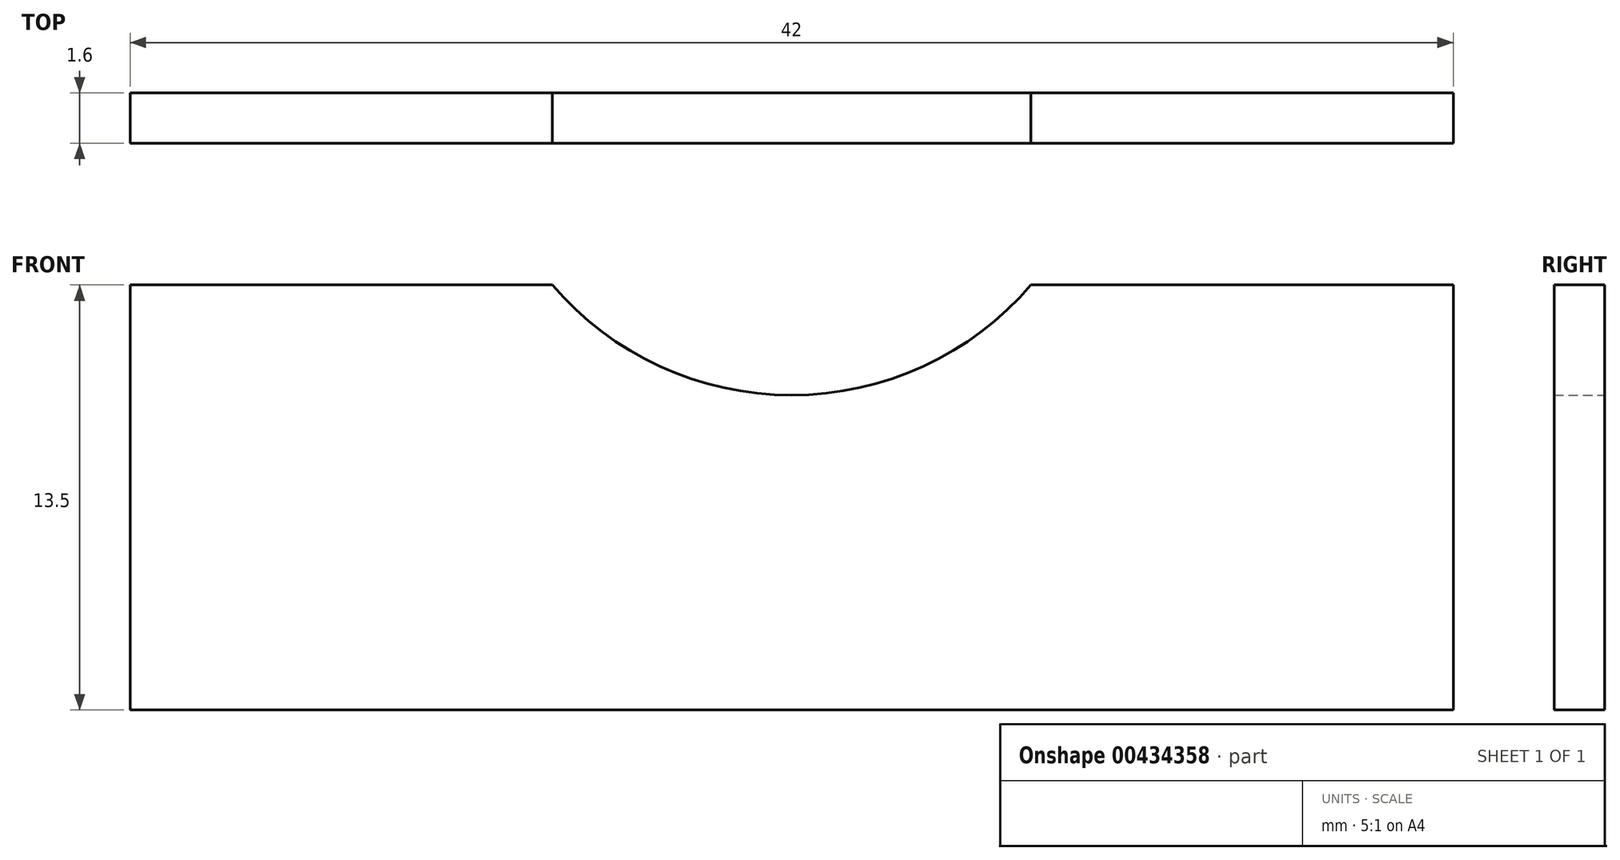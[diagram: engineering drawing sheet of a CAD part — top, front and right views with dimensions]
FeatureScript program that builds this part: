
annotation { "Feature Type Name" : "Feature", "Feature Type Description" : "" }
export const myFeature = defineFeature(function(context is Context, id is Id, definition is map)
    precondition{}
    {
        {
            var Q0;
            Q0=qCreatedBy(makeId("Front.planeOp"),FACE);
            var sketch = newSketch(context, id + "F0", { "sketchPlane" : qUnion([Q0])});
            skLineSegment(sketch, "E0.bottom", {"start": v(0, 0) * mm, "end": v(-42, 0) * mm});
            skLineSegment(sketch, "E0.top", {"start": v(0, 13.5) * mm, "end": v(-13.4, 13.5) * mm});
            skLineSegment(sketch, "E0.left", {"start": v(0, 0) * mm, "end": v(0, 13.5) * mm});
            skLineSegment(sketch, "E0.right", {"start": v(-42, 0) * mm, "end": v(-42, 13.5) * mm});
            skLineSegment(sketch, "E1", {"start": v(2.55, 20) * mm, "end": v(-47.21, 20) * mm, "construction": true});
            skArc(sketch, "E2", {"start": v(-28.6, 13.5) * mm, "mid": v(-21, 10) * mm, "end": v(-13.4, 13.5) * mm});
            skLineSegment(sketch, "E3.trimOffspring", {"start": v(-28.6, 13.5) * mm, "end": v(-42, 13.5) * mm});
            skSolve(sketch);
        }
        {
            var Q0;
            Q0=makeQuery(id+"F0.imprint","IMPRINT",FACE,{"disambiguationData":[TD([[makeQuery(id+"F0.imprint","IMPRINT",EDGE,{"derivedFrom":sQuery(id+"F0.wireOp",EDGE,"E0.bottom")}),-1.0]])]});
            extrude(context, id + "F1", {"entities" : qUnion([Q0]), "depth" : 1.6 * mm});
        }
    });
